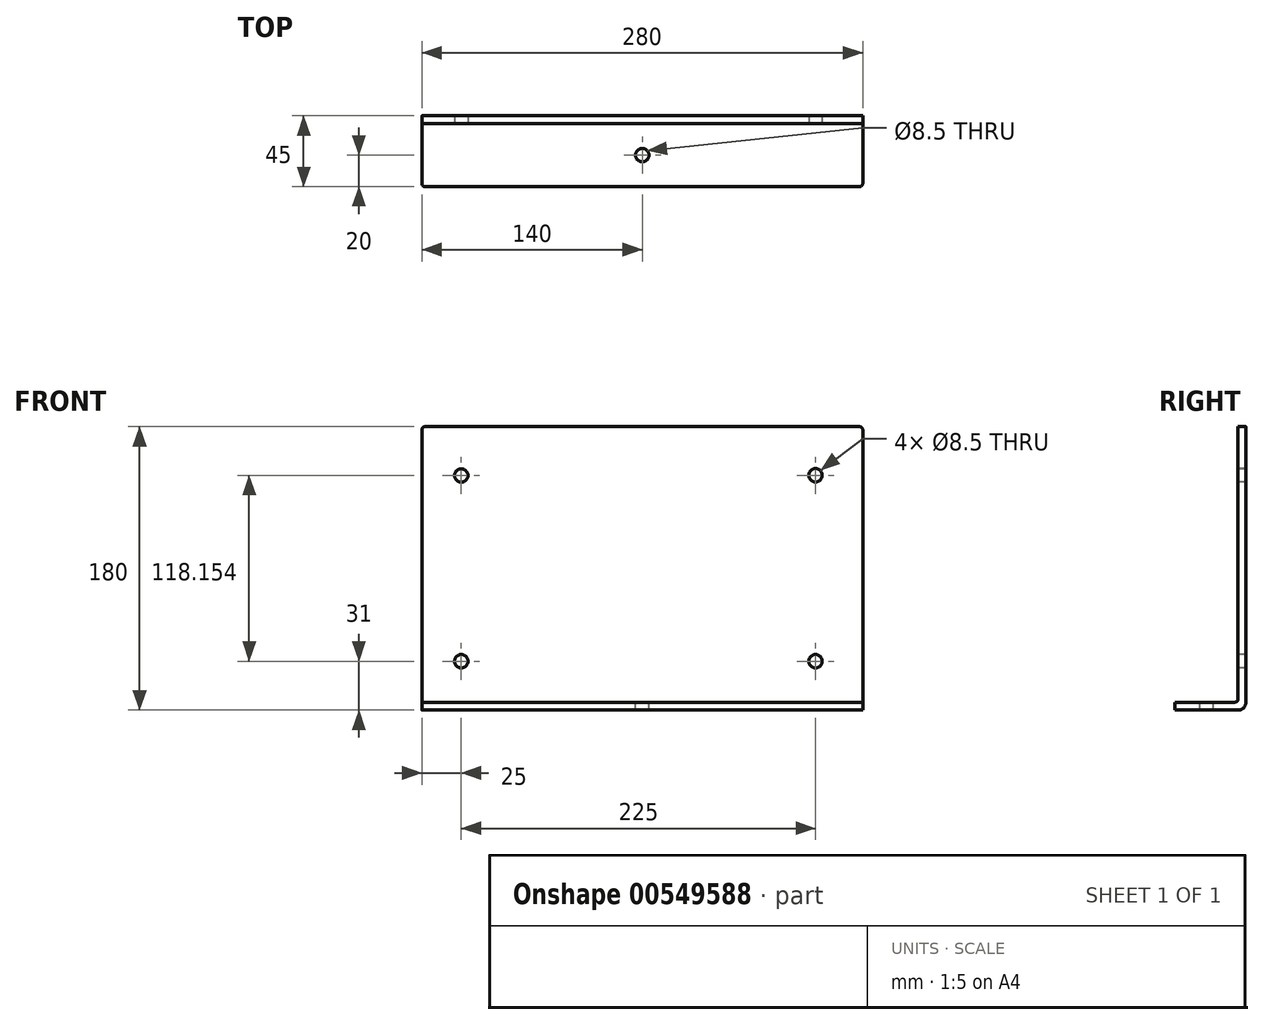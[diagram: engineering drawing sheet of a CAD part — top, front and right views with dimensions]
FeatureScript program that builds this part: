
annotation { "Feature Type Name" : "Feature", "Feature Type Description" : "" }
export const myFeature = defineFeature(function(context is Context, id is Id, definition is map)
    precondition{}
    {
        {
            var Q0;
            Q0=qCreatedBy(makeId("Right.planeOp"),FACE);
            var sketch = newSketch(context, id + "F0", { "sketchPlane" : qUnion([Q0])});
            skLineSegment(sketch, "E0", {"start": v(5, 87.5) * mm, "end": v(5, -92.5) * mm});
            skLineSegment(sketch, "E1", {"start": v(5, -92.5) * mm, "end": v(-40, -92.5) * mm});
            skLineSegment(sketch, "E2", {"start": v(-40, -92.5) * mm, "end": v(-40, -87.5) * mm});
            skLineSegment(sketch, "E3", {"start": v(-40, -87.5) * mm, "end": v(0, -87.5) * mm});
            skLineSegment(sketch, "E4", {"start": v(0, -87.5) * mm, "end": v(0, 87.5) * mm});
            skLineSegment(sketch, "E5", {"start": v(0, 87.5) * mm, "end": v(5, 87.5) * mm});
            skSolve(sketch);
        }
        {
            var Q0;
            Q0=makeQuery(id+"F0.imprint","IMPRINT",FACE,{"disambiguationData":[TD([[makeQuery(id+"F0.imprint","IMPRINT",EDGE,{"derivedFrom":sQuery(id+"F0.wireOp",EDGE,"E0")}),-1.0]])]});
            extrude(context, id + "F1", {"entities" : qUnion([Q0]), "depth" : 280 * mm, "offsetDistance" : 25 * mm});
        }
        {
            var Q0;
            Q0=makeQuery(id+"F1.opExtrude","SWEPT_FACE",FACE,{"disambiguationData":[OSD([sQuery(id+"F0.wireOp",EDGE,"E4")])]});
            var sketch = newSketch(context, id + "F2", { "sketchPlane" : qUnion([Q0])});
            skLineSegment(sketch, "E6", {"start": v(-85.83, 56.5) * mm, "end": v(367.73, 56.5) * mm, "construction": true});
            skLineSegment(sketch, "E7", {"start": v(-79.15, -61.5) * mm, "end": v(364.64, -61.5) * mm, "construction": true});
            skLineSegment(sketch, "E8", {"start": v(25, 56.5) * mm, "end": v(25, -68.82) * mm, "construction": true});
            skLineSegment(sketch, "E9", {"start": v(250, 56.65) * mm, "end": v(250, -73.94) * mm, "construction": true});
            skCircle(sketch, "E10", {"center": v(250, 56.65) * mm, "radius": 4.25 * mm});
            skCircle(sketch, "E11", {"center": v(250, -61.5) * mm, "radius": 4.25 * mm});
            skCircle(sketch, "E12", {"center": v(25, -61.5) * mm, "radius": 4.25 * mm});
            skCircle(sketch, "E13", {"center": v(25, 56.5) * mm, "radius": 4.25 * mm});
            skSolve(sketch);
        }
        {
            var Q0;
            Q0=makeQuery(id+"F2.imprint","IMPRINT",FACE,{"disambiguationData":[TD([[makeQuery(id+"F2.imprint","IMPRINT",EDGE,{"derivedFrom":sQuery(id+"F2.wireOp",EDGE,"E13")}),1.0]])]});
            var Q1;
            Q1=makeQuery(id+"F2.imprint","IMPRINT",FACE,{"disambiguationData":[TD([[makeQuery(id+"F2.imprint","IMPRINT",EDGE,{"derivedFrom":sQuery(id+"F2.wireOp",EDGE,"E10")}),1.0]])]});
            var Q2;
            Q2=makeQuery(id+"F2.imprint","IMPRINT",FACE,{"disambiguationData":[TD([[makeQuery(id+"F2.imprint","IMPRINT",EDGE,{"derivedFrom":sQuery(id+"F2.wireOp",EDGE,"E11")}),1.0]])]});
            var Q3;
            Q3=makeQuery(id+"F2.imprint","IMPRINT",FACE,{"disambiguationData":[TD([[makeQuery(id+"F2.imprint","IMPRINT",EDGE,{"derivedFrom":sQuery(id+"F2.wireOp",EDGE,"E12")}),1.0]])]});
            extrude(context, id + "F3", {"entities" : qUnion([Q0, Q1, Q2, Q3]), "operationType" : NewBodyOperationType.REMOVE, "endBound" : BoundingType.THROUGH_ALL, "oppositeDirection" : true, "depth" : 25 * mm, "offsetDistance" : 25 * mm});
        }
        {
            var Q0;
            Q0=makeQuery(id+"F1.opExtrude","CAP_EDGE",EDGE,{"disambiguationData":[OSD([sQuery(id+"F0.wireOp",EDGE,"E5")])],"isStart":false});
            var Q1;
            Q1=makeQuery(id+"F1.opExtrude","CAP_EDGE",EDGE,{"disambiguationData":[OSD([sQuery(id+"F0.wireOp",EDGE,"E5")])],"isStart":true});
            var Q2;
            Q2=makeQuery(id+"F1.opExtrude","CAP_EDGE",EDGE,{"disambiguationData":[OSD([sQuery(id+"F0.wireOp",EDGE,"E2")])],"isStart":true});
            var Q3;
            Q3=makeQuery(id+"F1.opExtrude","CAP_EDGE",EDGE,{"disambiguationData":[OSD([sQuery(id+"F0.wireOp",EDGE,"E2")])],"isStart":false});
            var Q4;
            Q4=makeQuery(id+"F1.opExtrude","SWEPT_EDGE",EDGE,{"disambiguationData":[OSD([sQuery(id+"F0.wireOp",EDGE,"E3"),sQuery(id+"F0.wireOp",EDGE,"E4")])]});
            fillet(context, id + "F4", {"entities" : qUnion([Q0, Q1, Q2, Q3, Q4]), "radius" : 2 * mm, "tangentPropagation" : true, "allowEdgeOverflow" : false});
        }
        {
            var Q0;
            Q0=makeQuery(id+"F1.opExtrude","SWEPT_EDGE",EDGE,{"disambiguationData":[OSD([sQuery(id+"F0.wireOp",EDGE,"E0"),sQuery(id+"F0.wireOp",EDGE,"E1")])]});
            fillet(context, id + "F5", {"entities" : qUnion([Q0]), "radius" : 5 * mm, "tangentPropagation" : true, "allowEdgeOverflow" : false});
        }
        {
            var Q0;
            Q0=makeQuery(id+"F1.opExtrude","SWEPT_FACE",FACE,{"disambiguationData":[OSD([sQuery(id+"F0.wireOp",EDGE,"E3")])]});
            var sketch = newSketch(context, id + "F6", { "sketchPlane" : qUnion([Q0])});
            skLineSegment(sketch, "E14", {"start": v(-54.71, -20) * mm, "end": v(329.93, -20) * mm, "construction": true});
            skCircle(sketch, "E15", {"center": v(140, -20) * mm, "radius": 4.25 * mm});
            skPoint(sketch, "E15.centerSnap0", {"position": v(140, -2) * mm});
            skSolve(sketch);
        }
        {
            var Q0;
            Q0=makeQuery(id+"F6.imprint","IMPRINT",FACE,{"disambiguationData":[TD([[makeQuery(id+"F6.imprint","IMPRINT",EDGE,{"derivedFrom":sQuery(id+"F6.wireOp",EDGE,"E15")}),1.0]])]});
            extrude(context, id + "F7", {"entities" : qUnion([Q0]), "operationType" : NewBodyOperationType.REMOVE, "endBound" : BoundingType.THROUGH_ALL, "oppositeDirection" : true, "depth" : 25 * mm, "offsetDistance" : 25 * mm});
        }
    });
